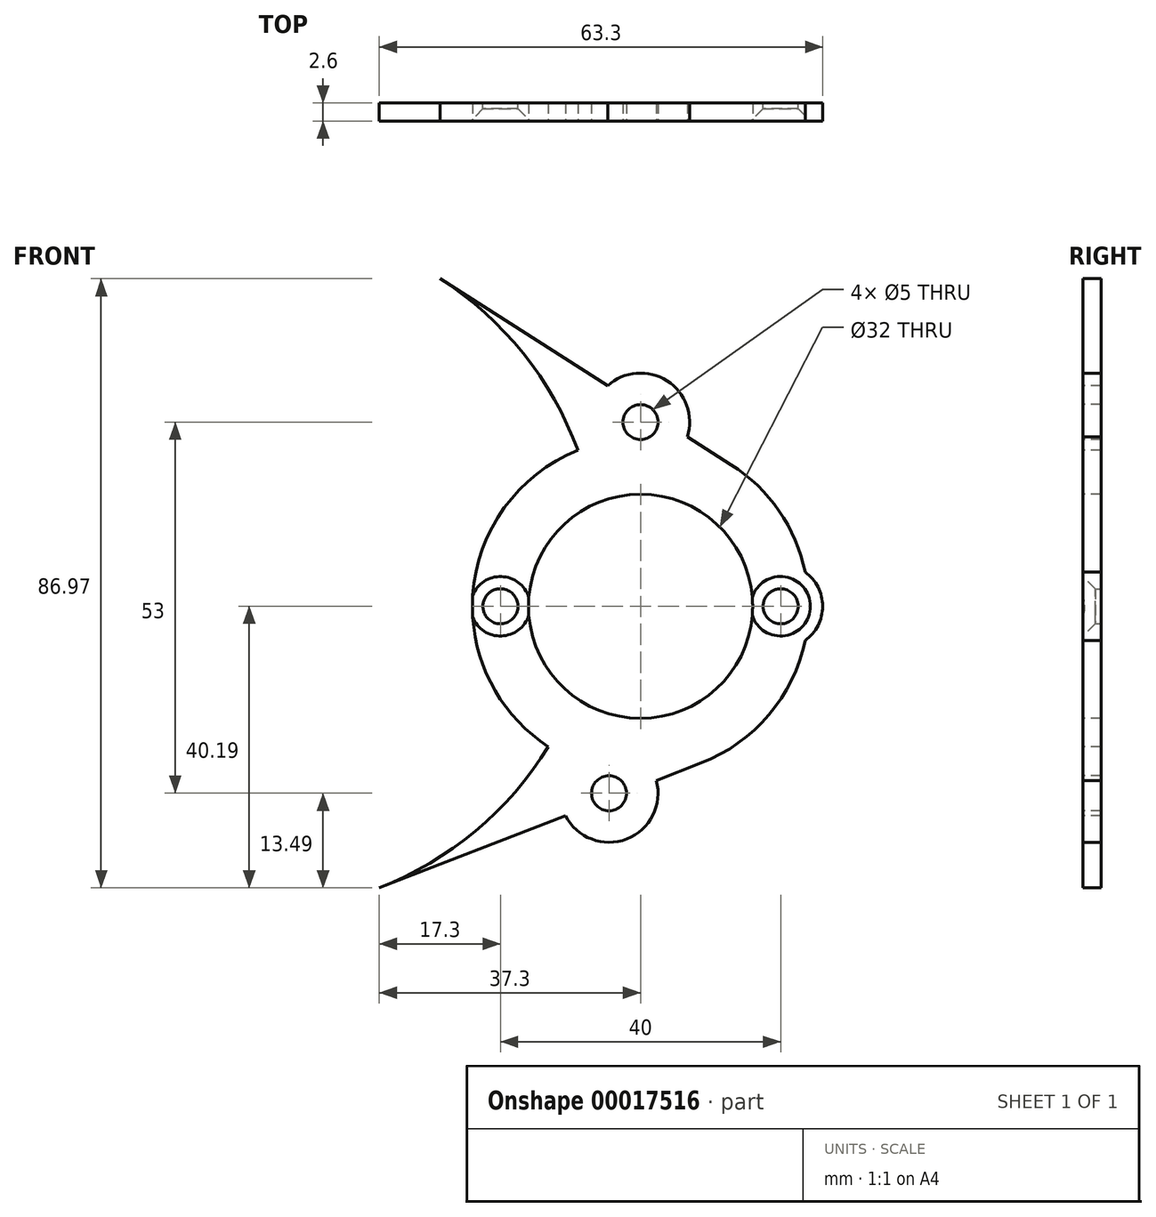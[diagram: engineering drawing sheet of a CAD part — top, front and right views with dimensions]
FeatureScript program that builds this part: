
annotation { "Feature Type Name" : "Feature", "Feature Type Description" : "" }
export const myFeature = defineFeature(function(context is Context, id is Id, definition is map)
    precondition{}
    {
        {
            var Q0;
            Q0=qCreatedBy(makeId("Front.planeOp"),FACE);
            var sketch = newSketch(context, id + "F0", { "sketchPlane" : qUnion([Q0])});
            skLineSegment(sketch, "E0", {"start": v(20, 0) * mm, "end": v(-79.3, 0) * mm, "construction": true});
            skLineSegment(sketch, "E1.bottom", {"start": v(-30.7, 19) * mm, "end": v(-79.3, 19) * mm});
            skLineSegment(sketch, "E1.top", {"start": v(-30.7, 49) * mm, "end": v(-79.3, 49) * mm});
            skLineSegment(sketch, "E1.left", {"start": v(-30.7, 19) * mm, "end": v(-30.7, 49) * mm});
            skLineSegment(sketch, "E1.right", {"start": v(-79.3, 19) * mm, "end": v(-79.3, 49) * mm});
            skPoint(sketch, "E1.middle", {"position": v(-55, 34) * mm});
            skLineSegment(sketch, "E2", {"start": v(-29, -29) * mm, "end": v(-29, 29) * mm, "construction": true});
            skLineSegment(sketch, "E3", {"start": v(-55, 5.5) * mm, "end": v(-55, 34) * mm, "construction": true});
            skCircle(sketch, "E4", {"center": v(-55, 5.5) * mm, "radius": 10.5 * mm});
            skCircle(sketch, "E5", {"center": v(-55, 5.5) * mm, "radius": 6 * mm, "construction": true});
            skLineSegment(sketch, "E6", {"start": v(0, 0) * mm, "end": v(0, 26.3) * mm, "construction": true});
            skCircle(sketch, "E7", {"center": v(0, 0) * mm, "radius": 16 * mm});
            skCircle(sketch, "E8", {"center": v(0, 26.3) * mm, "radius": 2.5 * mm});
            skCircle(sketch, "E9", {"center": v(20, 0) * mm, "radius": 2.5 * mm});
            skCircle(sketch, "E10.MirrorC", {"center": v(-20, 0) * mm, "radius": 2.5 * mm});
            skCircle(sketch, "E11", {"center": v(-29, 29) * mm, "radius": 3 * mm});
            skCircle(sketch, "E12.MirrorC", {"center": v(-29, -29) * mm, "radius": 3 * mm});
            skLineSegment(sketch, "E13", {"start": v(-4.5, 0) * mm, "end": v(-4.5, -26.7) * mm, "construction": true});
            skCircle(sketch, "E14", {"center": v(-4.5, -26.7) * mm, "radius": 2.5 * mm});
            skSolve(sketch);
        }
        {
            var Q0;
            Q0=qCreatedBy(makeId("Front.planeOp"),FACE);
            var sketch = newSketch(context, id + "F1", { "sketchPlane" : qUnion([Q0])});
            skCircle(sketch, "E15", {"center": v(-55, 5.5) * mm, "radius": 49 * mm});
            skCircle(sketch, "E16", {"center": v(0, 0) * mm, "radius": 24 * mm});
            skLineSegment(sketch, "E17", {"start": v(-28.6, 46.78) * mm, "end": v(12.93, 20.22) * mm});
            skLineSegment(sketch, "E18", {"start": v(-37.3, -40.2) * mm, "end": v(8.67, -22.38) * mm});
            skCircle(sketch, "E19", {"center": v(0, 26.3) * mm, "radius": 7 * mm});
            skCircle(sketch, "E20", {"center": v(20, 0) * mm, "radius": 6 * mm});
            skCircle(sketch, "E21", {"center": v(-4.5, -26.7) * mm, "radius": 7 * mm});
            skCircle(sketch, "E22.0", {"center": v(-55, 5.5) * mm, "radius": 10.5 * mm});
            skCircle(sketch, "E23.0", {"center": v(0, 26.3) * mm, "radius": 2.5 * mm});
            skCircle(sketch, "E23.1", {"center": v(-4.5, -26.7) * mm, "radius": 2.5 * mm});
            skLineSegment(sketch, "E24.0", {"start": v(-79.3, 19) * mm, "end": v(-79.3, 49) * mm});
            skLineSegment(sketch, "E24.1", {"start": v(-30.7, 19) * mm, "end": v(-79.3, 19) * mm});
            skLineSegment(sketch, "E24.2", {"start": v(-30.7, 19) * mm, "end": v(-30.7, 49) * mm});
            skCircle(sketch, "E25.0", {"center": v(0, 0) * mm, "radius": 16 * mm});
            skCircle(sketch, "E26.0", {"center": v(-29, 29) * mm, "radius": 3 * mm});
            skCircle(sketch, "E26.1", {"center": v(-29, -29) * mm, "radius": 3 * mm});
            skSolve(sketch);
        }
        {
            var Q0;
            {var subQ0=sQuery(id+"F1.wireOp",EDGE,"E20");var subQ1=sQuery(id+"F1.wireOp",EDGE,"E16");var subQ2=makeQuery(id+"F1.imprint","INTERSECT",VERTEX,{"disambiguationData":[OD(0.0)],"derivedFrom":[subQ1,subQ0]});Q0=makeQuery(id+"F1.imprint","IMPRINT",FACE,{"disambiguationData":[TD([[makeQuery(id+"F1.imprint","IMPRINT",EDGE,{"disambiguationData":[TD([[subQ2,1.0]])],"derivedFrom":subQ1}),-1.0]])]});}
            var Q1;
            {var subQ0=sQuery(id+"F1.wireOp",EDGE,"E17");var subQ1=sQuery(id+"F1.wireOp",EDGE,"E16");var subQ2=makeQuery(id+"F1.imprint","INTERSECT",VERTEX,{"derivedFrom":[subQ1,subQ0]});Q1=makeQuery(id+"F1.imprint","IMPRINT",FACE,{"disambiguationData":[TD([[makeQuery(id+"F1.imprint","IMPRINT",EDGE,{"disambiguationData":[TD([[subQ2,-1.0]])],"derivedFrom":subQ1}),-1.0]])]});}
            var Q2;
            {var subQ0=sQuery(id+"F1.wireOp",EDGE,"E18");var subQ1=sQuery(id+"F1.wireOp",EDGE,"E16");var subQ2=makeQuery(id+"F1.imprint","INTERSECT",VERTEX,{"derivedFrom":[subQ1,subQ0]});Q2=makeQuery(id+"F1.imprint","IMPRINT",FACE,{"disambiguationData":[TD([[makeQuery(id+"F1.imprint","IMPRINT",EDGE,{"disambiguationData":[TD([[subQ2,1.0]])],"derivedFrom":subQ1}),-1.0]])]});}
            var Q3;
            {var subQ0=sQuery(id+"F1.wireOp",EDGE,"E21");var subQ1=sQuery(id+"F1.wireOp",EDGE,"E18");var subQ2=makeQuery(id+"F1.imprint","INTERSECT",VERTEX,{"disambiguationData":[OD(0.0)],"derivedFrom":[subQ1,subQ0]});Q3=makeQuery(id+"F1.imprint","IMPRINT",FACE,{"disambiguationData":[TD([[makeQuery(id+"F1.imprint","IMPRINT",EDGE,{"disambiguationData":[TD([[subQ2,-1.0]])],"derivedFrom":subQ1}),-1.0]])]});}
            var Q4;
            {var subQ0=sQuery(id+"F1.wireOp",EDGE,"E17");var subQ1=sQuery(id+"F1.wireOp",EDGE,"E15");var subQ2=makeQuery(id+"F1.imprint","INTERSECT",VERTEX,{"derivedFrom":[subQ1,subQ0]});Q4=makeQuery(id+"F1.imprint","IMPRINT",FACE,{"disambiguationData":[TD([[makeQuery(id+"F1.imprint","IMPRINT",EDGE,{"disambiguationData":[TD([[subQ2,1.0]])],"derivedFrom":subQ1}),-1.0]])]});}
            var Q5;
            {var subQ0=sQuery(id+"F1.wireOp",EDGE,"E18");var subQ1=sQuery(id+"F1.wireOp",EDGE,"E15");var subQ2=makeQuery(id+"F1.imprint","INTERSECT",VERTEX,{"derivedFrom":[subQ1,subQ0]});Q5=makeQuery(id+"F1.imprint","IMPRINT",FACE,{"disambiguationData":[TD([[makeQuery(id+"F1.imprint","IMPRINT",EDGE,{"disambiguationData":[TD([[subQ2,-1.0]])],"derivedFrom":subQ1}),-1.0]])]});}
            var Q6;
            {var subQ0=sQuery(id+"F1.wireOp",EDGE,"E19");var subQ1=sQuery(id+"F1.wireOp",EDGE,"E17");var subQ2=makeQuery(id+"F1.imprint","INTERSECT",VERTEX,{"disambiguationData":[OD(0.0)],"derivedFrom":[subQ1,subQ0]});Q6=makeQuery(id+"F1.imprint","IMPRINT",FACE,{"disambiguationData":[TD([[makeQuery(id+"F1.imprint","IMPRINT",EDGE,{"disambiguationData":[TD([[subQ2,-1.0]])],"derivedFrom":subQ1}),1.0]])]});}
            var Q7;
            {var subQ0=sQuery(id+"F1.wireOp",EDGE,"E19");var subQ1=sQuery(id+"F1.wireOp",EDGE,"E16");var subQ2=makeQuery(id+"F1.imprint","INTERSECT",VERTEX,{"disambiguationData":[OD(0.0)],"derivedFrom":[subQ1,subQ0]});Q7=makeQuery(id+"F1.imprint","IMPRINT",FACE,{"disambiguationData":[TD([[makeQuery(id+"F1.imprint","IMPRINT",EDGE,{"disambiguationData":[TD([[subQ2,-1.0]])],"derivedFrom":subQ1}),-1.0]])]});}
            var Q8;
            {var subQ0=sQuery(id+"F1.wireOp",EDGE,"E23.0");var subQ1=sQuery(id+"F1.wireOp",EDGE,"E16");var subQ2=makeQuery(id+"F1.imprint","INTERSECT",VERTEX,{"disambiguationData":[OD(1.0)],"derivedFrom":[subQ1,subQ0]});Q8=makeQuery(id+"F1.imprint","IMPRINT",FACE,{"disambiguationData":[TD([[makeQuery(id+"F1.imprint","IMPRINT",EDGE,{"disambiguationData":[TD([[subQ2,-1.0]])],"derivedFrom":subQ1}),-1.0]])]});}
            var Q9;
            {var subQ0=sQuery(id+"F1.wireOp",EDGE,"E20");var subQ1=sQuery(id+"F1.wireOp",EDGE,"E16");var subQ2=makeQuery(id+"F1.imprint","INTERSECT",VERTEX,{"disambiguationData":[OD(0.0)],"derivedFrom":[subQ1,subQ0]});Q9=makeQuery(id+"F1.imprint","IMPRINT",FACE,{"disambiguationData":[TD([[makeQuery(id+"F1.imprint","IMPRINT",EDGE,{"disambiguationData":[TD([[subQ2,1.0]])],"derivedFrom":subQ1}),1.0]])]});}
            var Q10;
            Q10=makeQuery(id+"F1.imprint","IMPRINT",FACE,{"disambiguationData":[TD([[makeQuery(id+"F1.imprint","IMPRINT",EDGE,{"derivedFrom":sQuery(id+"F1.wireOp",EDGE,"E22.0")}),-1.0]])]});
            var Q11;
            {var subQ0=sQuery(id+"F1.wireOp",EDGE,"E21");var subQ3=sQuery(id+"F1.wireOp",EDGE,"E16");var subQ9=makeQuery(id+"F1.imprint","INTERSECT",VERTEX,{"disambiguationData":[OD(0.0)],"derivedFrom":[subQ3,subQ0]});Q11=makeQuery(id+"F1.imprint","IMPRINT",FACE,{"disambiguationData":[TD([[makeQuery(id+"F1.imprint","IMPRINT",EDGE,{"disambiguationData":[TD([[subQ9,-1.0]])],"derivedFrom":subQ3}),-1.0]])]});}
            var Q12;
            {var subQ0=sQuery(id+"F1.wireOp",EDGE,"E19");var subQ1=sQuery(id+"F1.wireOp",EDGE,"E16");var subQ2=makeQuery(id+"F1.imprint","INTERSECT",VERTEX,{"disambiguationData":[OD(0.0)],"derivedFrom":[subQ1,subQ0]});Q12=makeQuery(id+"F1.imprint","IMPRINT",FACE,{"disambiguationData":[TD([[makeQuery(id+"F1.imprint","IMPRINT",EDGE,{"disambiguationData":[TD([[subQ2,-1.0]])],"derivedFrom":subQ1}),1.0]])]});}
            var Q13;
            {var subQ0=sQuery(id+"F1.wireOp",EDGE,"E16");var subQ4=sQuery(id+"F1.wireOp",EDGE,"E15");var subQ5=makeQuery(id+"F1.imprint","INTERSECT",VERTEX,{"disambiguationData":[OD(0.0)],"derivedFrom":[subQ4,subQ0]});Q13=makeQuery(id+"F1.imprint","IMPRINT",FACE,{"disambiguationData":[TD([[makeQuery(id+"F1.imprint","IMPRINT",EDGE,{"disambiguationData":[TD([[subQ5,1.0]])],"derivedFrom":subQ4}),-1.0]])]});}
            var Q14;
            {var subQ0=sQuery(id+"F1.wireOp",EDGE,"E16");var subQ4=sQuery(id+"F1.wireOp",EDGE,"E15");var subQ5=makeQuery(id+"F1.imprint","INTERSECT",VERTEX,{"disambiguationData":[OD(1.0)],"derivedFrom":[subQ4,subQ0]});Q14=makeQuery(id+"F1.imprint","IMPRINT",FACE,{"disambiguationData":[TD([[makeQuery(id+"F1.imprint","IMPRINT",EDGE,{"disambiguationData":[TD([[subQ5,-1.0]])],"derivedFrom":subQ4}),-1.0]])]});}
            var Q15;
            {var subQ0=sQuery(id+"F1.wireOp",EDGE,"E21");var subQ1=sQuery(id+"F1.wireOp",EDGE,"E16");var subQ2=makeQuery(id+"F1.imprint","INTERSECT",VERTEX,{"disambiguationData":[OD(0.0)],"derivedFrom":[subQ1,subQ0]});Q15=makeQuery(id+"F1.imprint","IMPRINT",FACE,{"disambiguationData":[TD([[makeQuery(id+"F1.imprint","IMPRINT",EDGE,{"disambiguationData":[TD([[subQ2,-1.0]])],"derivedFrom":subQ1}),1.0]])]});}
            var Q16;
            {var subQ0=sQuery(id+"F1.wireOp",EDGE,"E16");var subQ1=sQuery(id+"F1.wireOp",EDGE,"E15");var subQ2=makeQuery(id+"F1.imprint","INTERSECT",VERTEX,{"disambiguationData":[OD(0.0)],"derivedFrom":[subQ1,subQ0]});Q16=makeQuery(id+"F1.imprint","IMPRINT",FACE,{"disambiguationData":[TD([[makeQuery(id+"F1.imprint","IMPRINT",EDGE,{"disambiguationData":[TD([[subQ2,1.0]])],"derivedFrom":subQ1}),1.0]])]});}
            extrude(context, id + "F2", {"entities" : qUnion([Q0, Q1, Q2, Q3, Q4, Q5, Q6, Q7, Q8, Q9, Q10, Q11, Q12, Q13, Q14, Q15, Q16]), "oppositeDirection" : true, "depth" : 2.6 * mm});
        }
        {
            var Q0;
            Q0=sQuery(id+"F0.wireOp",VERTEX,"E9.center");
            var Q1;
            Q1=sQuery(id+"F0.wireOp",VERTEX,"E10.MirrorC.center");
            var Q2;
            Q2=makeQuery(id+"F2.opExtrude","SWEPT_BODY",BODY,{"disambiguationData":[OSD([sQuery(id+"F1.wireOp",EDGE,"E15"),sQuery(id+"F1.wireOp",EDGE,"E16"),sQuery(id+"F1.wireOp",EDGE,"E17"),sQuery(id+"F1.wireOp",EDGE,"E18"),sQuery(id+"F1.wireOp",EDGE,"E19"),sQuery(id+"F1.wireOp",EDGE,"E20"),sQuery(id+"F1.wireOp",EDGE,"E21"),sQuery(id+"F1.wireOp",EDGE,"E22.0"),sQuery(id+"F1.wireOp",EDGE,"E23.0"),sQuery(id+"F1.wireOp",EDGE,"E23.1"),sQuery(id+"F1.wireOp",EDGE,"E24.0"),sQuery(id+"F1.wireOp",EDGE,"E24.1"),sQuery(id+"F1.wireOp",EDGE,"E24.2"),sQuery(id+"F1.wireOp",EDGE,"E25.0")])]});
            hole(context, id + "F3", {"style" : HoleStyle.C_SINK, "endStyle" : HoleEndStyle.BLIND, "holeDiameter" : 5 * mm, "cSinkDiameter" : 8.5 * mm, "cSinkAngle" : 90 * degree, "holeDepth" : 60 * mm, "locations" : qUnion([Q0, Q1]), "scope" : qUnion([Q2]), "startStyle" : HoleStartStyle.SKETCH});
        }
    });
